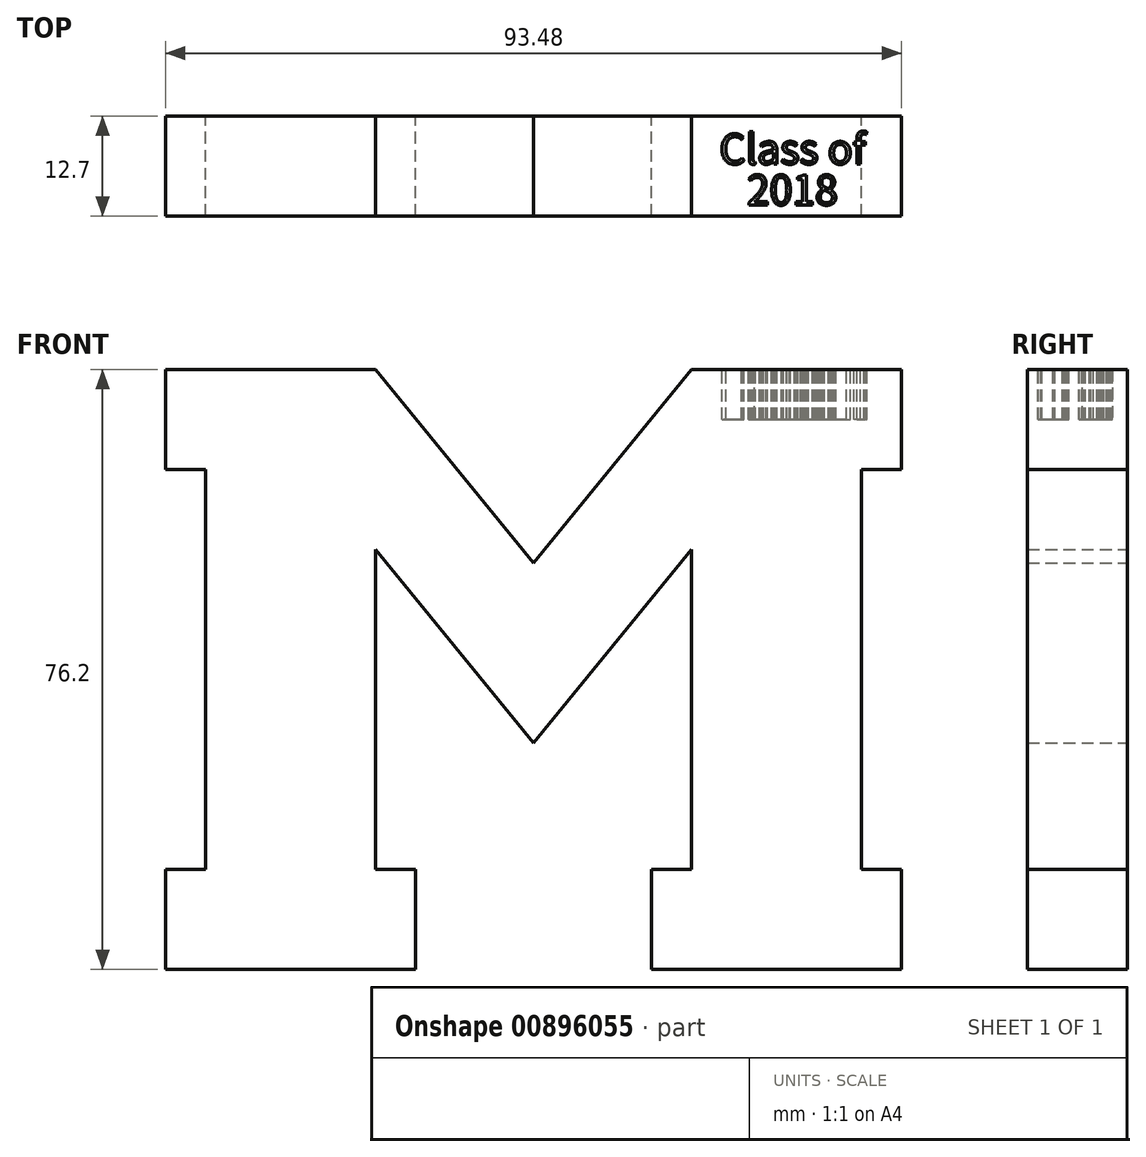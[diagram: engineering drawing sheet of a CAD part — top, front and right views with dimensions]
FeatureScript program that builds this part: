
annotation { "Feature Type Name" : "Feature", "Feature Type Description" : "" }
export const myFeature = defineFeature(function(context is Context, id is Id, definition is map)
    precondition{}
    {
        {
            var Q0;
            Q0=qCreatedBy(makeId("Front.planeOp"),FACE);
            var sketch = newSketch(context, id + "F0", { "sketchPlane" : qUnion([Q0])});
            skLineSegment(sketch, "E0", {"start": v(-46.74, -28.74) * mm, "end": v(-15, -28.74) * mm});
            skLineSegment(sketch, "E1", {"start": v(-46.74, -28.74) * mm, "end": v(-46.74, -16.04) * mm});
            skLineSegment(sketch, "E2", {"start": v(-46.74, -16.04) * mm, "end": v(-41.66, -16.04) * mm});
            skLineSegment(sketch, "E3", {"start": v(-15, -28.74) * mm, "end": v(-15, -16.04) * mm});
            skLineSegment(sketch, "E4", {"start": v(-15, -16.04) * mm, "end": v(-20.07, -16.04) * mm});
            skLineSegment(sketch, "E5", {"start": v(-20.07, -16.04) * mm, "end": v(-20.07, 24.6) * mm});
            skLineSegment(sketch, "E6", {"start": v(-20.07, 24.6) * mm, "end": v(0, 0) * mm});
            skLineSegment(sketch, "E7", {"start": v(0, 0) * mm, "end": v(20.07, 24.6) * mm});
            skLineSegment(sketch, "E8", {"start": v(20.07, 24.6) * mm, "end": v(20.07, -16.04) * mm});
            skLineSegment(sketch, "E9", {"start": v(20.07, -16.04) * mm, "end": v(15, -16.04) * mm});
            skLineSegment(sketch, "E10", {"start": v(15, -16.04) * mm, "end": v(15, -28.74) * mm});
            skLineSegment(sketch, "E11", {"start": v(15, -28.74) * mm, "end": v(46.74, -28.74) * mm});
            skLineSegment(sketch, "E12", {"start": v(46.74, -28.74) * mm, "end": v(46.74, -16.04) * mm});
            skLineSegment(sketch, "E13", {"start": v(46.74, -16.04) * mm, "end": v(41.66, -16.04) * mm});
            skLineSegment(sketch, "E14", {"start": v(41.66, 47.46) * mm, "end": v(20.07, 47.46) * mm});
            skLineSegment(sketch, "E15", {"start": v(20.07, 47.46) * mm, "end": v(0, 22.86) * mm});
            skLineSegment(sketch, "E16", {"start": v(0, 22.86) * mm, "end": v(-20.07, 47.46) * mm});
            skLineSegment(sketch, "E17", {"start": v(-20.07, 47.46) * mm, "end": v(-41.66, 47.46) * mm});
            skLineSegment(sketch, "E18", {"start": v(-41.66, -16.04) * mm, "end": v(-41.66, 34.76) * mm});
            skLineSegment(sketch, "E19", {"start": v(-41.66, 34.76) * mm, "end": v(-46.74, 34.76) * mm});
            skLineSegment(sketch, "E20", {"start": v(-46.74, 34.76) * mm, "end": v(-46.74, 47.46) * mm});
            skLineSegment(sketch, "E21", {"start": v(-46.74, 47.46) * mm, "end": v(-41.66, 47.46) * mm});
            skLineSegment(sketch, "E22", {"start": v(41.66, -16.04) * mm, "end": v(41.66, 34.76) * mm});
            skLineSegment(sketch, "E23", {"start": v(41.66, 34.76) * mm, "end": v(46.74, 34.76) * mm});
            skLineSegment(sketch, "E24", {"start": v(46.74, 34.76) * mm, "end": v(46.74, 47.46) * mm});
            skLineSegment(sketch, "E25", {"start": v(46.74, 47.46) * mm, "end": v(41.66, 47.46) * mm});
            skPoint(sketch, "E26", {"position": v(-44.2, 47.46) * mm});
            skSolve(sketch);
        }
        {
            var Q0;
            Q0=makeQuery(id+"F0.imprint","IMPRINT",FACE,{"disambiguationData":[TD([[makeQuery(id+"F0.imprint","IMPRINT",EDGE,{"derivedFrom":sQuery(id+"F0.wireOp",EDGE,"E0")}),1.0]])]});
            extrude(context, id + "F1", {"entities" : qUnion([Q0]), "depth" : 12.7 * mm, "offsetDistance" : 25.4 * mm});
        }
        {
            var Q0;
            Q0=makeQuery(id+"F1.opExtrude","SWEPT_FACE",FACE,{"disambiguationData":[OSD([sQuery(id+"F0.wireOp",EDGE,"E14"),sQuery(id+"F0.wireOp",EDGE,"E25")])]});
            var sketch = newSketch(context, id + "F2", { "sketchPlane" : qUnion([Q0])});
            skText(sketch, "E27", { "text": "Class of\n   2018", "fontName": "NotoSansCJKjp-Regular.otf"});
            const initialGuessF2  = {"E27": [0.02362, -0.00609, 1, 0, 0.00374]};
            skSetInitialGuess(sketch, initialGuessF2);
            skSolve(sketch);
        }
        {
            var Q0;
            Q0 = qSketchRegion(id + "F2", true);
            extrude(context, id + "F3", {"entities" : qUnion([Q0]), "operationType" : NewBodyOperationType.REMOVE, "oppositeDirection" : true, "depth" : 6.35 * mm, "offsetDistance" : 25.4 * mm});
        }
    });
